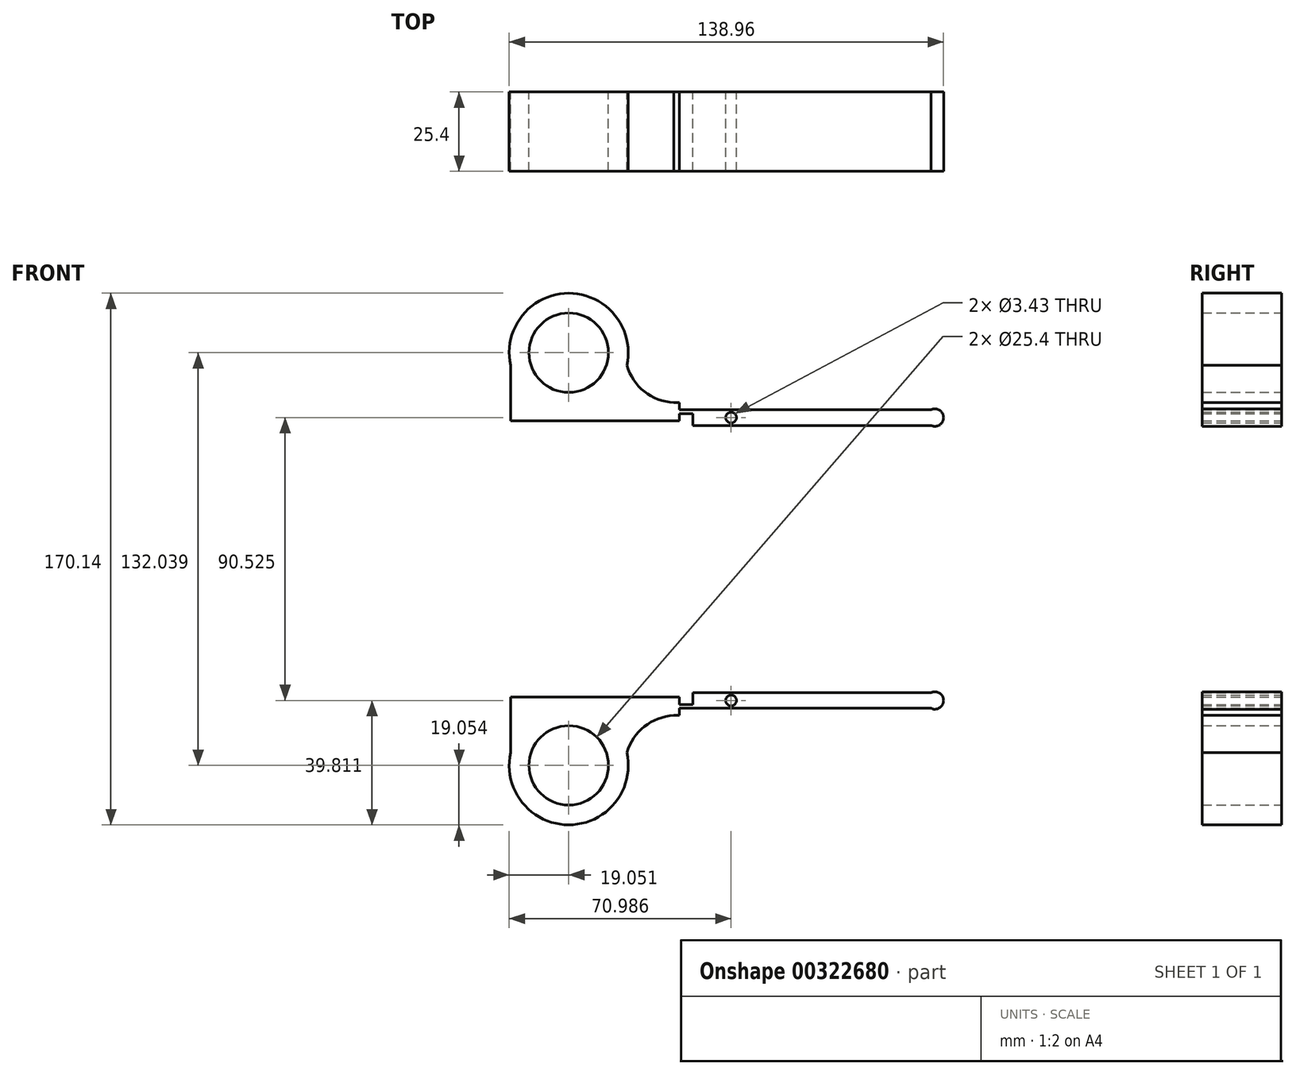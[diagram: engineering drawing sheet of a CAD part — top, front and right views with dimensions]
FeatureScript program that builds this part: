
annotation { "Feature Type Name" : "Feature", "Feature Type Description" : "" }
export const myFeature = defineFeature(function(context is Context, id is Id, definition is map)
    precondition{}
    {
        {
            var Q0;
            Q0=qCreatedBy(makeId("Front.planeOp"),FACE);
            var sketch = newSketch(context, id + "F0", { "sketchPlane" : qUnion([Q0])});
            skLineSegment(sketch, "E0", {"start": v(-58.3, -14.66) * mm, "end": v(-4.32, -14.66) * mm});
            skLineSegment(sketch, "E1", {"start": v(-4.32, -14.66) * mm, "end": v(-58.3, -14.66) * mm});
            skLineSegment(sketch, "E2", {"start": v(-58.3, 3.12) * mm, "end": v(-58.3, -14.66) * mm});
            skArc(sketch, "E3", {"start": v(-21.07, 3.12) * mm, "mid": v(-39.68, 26.22) * mm, "end": v(-58.3, 3.12) * mm});
            skArc(sketch, "E4", {"start": v(-21.07, 3.12) * mm, "mid": v(-14.77, -5.76) * mm, "end": v(-4.32, -8.8) * mm});
            skLineSegment(sketch, "E5", {"start": v(-4.32, -14.66) * mm, "end": v(-4.32, -8.8) * mm});
            skCircle(sketch, "E6", {"center": v(-39.68, 7.17) * mm, "radius": 12.7 * mm});
            skLineSegment(sketch, "E7", {"start": v(-4.32, -8.8) * mm, "end": v(-25.78, -8.8) * mm});
            skLineSegment(sketch, "E8", {"start": v(-4.32, -11.08) * mm, "end": v(76.2, -11.08) * mm});
            skPoint(sketch, "E9.endSnap0", {"position": v(-4.32, -11.73) * mm});
            skArc(sketch, "E10", {"start": v(76.2, -16.09) * mm, "mid": v(80.23, -13.58) * mm, "end": v(76.2, -11.08) * mm});
            skCircle(sketch, "E11", {"center": v(12.26, -13.58) * mm, "radius": 1.71 * mm});
            skLineSegment(sketch, "E12", {"start": v(13.97, -13.55) * mm, "end": v(45.9, -13.55) * mm});
            skLineSegment(sketch, "E13", {"start": v(76.2, -16.09) * mm, "end": v(0, -16.09) * mm});
            skLineSegment(sketch, "E14", {"start": v(0, -16.09) * mm, "end": v(0, -12.28) * mm});
            skLineSegment(sketch, "E15", {"start": v(0, -12.28) * mm, "end": v(-4.32, -12.28) * mm});
            skLineSegment(sketch, "E16.MirrorCS", {"start": v(-4.32, -103.03) * mm, "end": v(-58.3, -103.03) * mm});
            skLineSegment(sketch, "E17.MirrorCS", {"start": v(-58.3, -120.81) * mm, "end": v(-58.3, -103.03) * mm});
            skArc(sketch, "E18.MirrorCS", {"start": v(-21.07, -120.81) * mm, "mid": v(-39.68, -143.92) * mm, "end": v(-58.3, -120.81) * mm});
            skCircle(sketch, "E19.MirrorC", {"center": v(-39.68, -124.87) * mm, "radius": 12.7 * mm});
            skArc(sketch, "E20.MirrorCS", {"start": v(-21.07, -120.81) * mm, "mid": v(-14.77, -111.93) * mm, "end": v(-4.32, -108.9) * mm});
            skLineSegment(sketch, "E21.MirrorCS", {"start": v(-4.32, -108.9) * mm, "end": v(-25.78, -108.9) * mm});
            skLineSegment(sketch, "E22.MirrorCS", {"start": v(-4.32, -106.61) * mm, "end": v(76.2, -106.61) * mm});
            skLineSegment(sketch, "E23.MirrorCS", {"start": v(0, -105.41) * mm, "end": v(-4.32, -105.41) * mm});
            skLineSegment(sketch, "E24.MirrorCS", {"start": v(-4.32, -103.03) * mm, "end": v(-4.32, -108.9) * mm});
            skLineSegment(sketch, "E25.MirrorCS", {"start": v(0, -101.6) * mm, "end": v(0, -105.41) * mm});
            skLineSegment(sketch, "E26.MirrorCS", {"start": v(76.2, -101.6) * mm, "end": v(0, -101.6) * mm});
            skCircle(sketch, "E27.MirrorC", {"center": v(12.26, -104.1) * mm, "radius": 1.71 * mm});
            skLineSegment(sketch, "E28.MirrorCS", {"start": v(13.97, -104.14) * mm, "end": v(45.9, -104.14) * mm});
            skArc(sketch, "E29.MirrorCS", {"start": v(76.2, -101.6) * mm, "mid": v(80.23, -104.1) * mm, "end": v(76.2, -106.61) * mm});
            skSolve(sketch);
        }
        {
            var Q0;
            Q0 = qSketchRegion(id + "F0", true);
            var Q1;
            {var subQ4=sQuery(id+"F0.wireOp",EDGE,"E1");Q1=makeQuery(id+"F0.imprint","IMPRINT",FACE,{"disambiguationData":[TD([[makeQuery(id+"F0.imprint","IMPRINT",EDGE,{"derivedFrom":subQ4}),-1.0]])]});}
            extrude(context, id + "F1", {"entities" : qUnion([Q0, Q1]), "depth" : 25.4 * mm});
        }
    });
